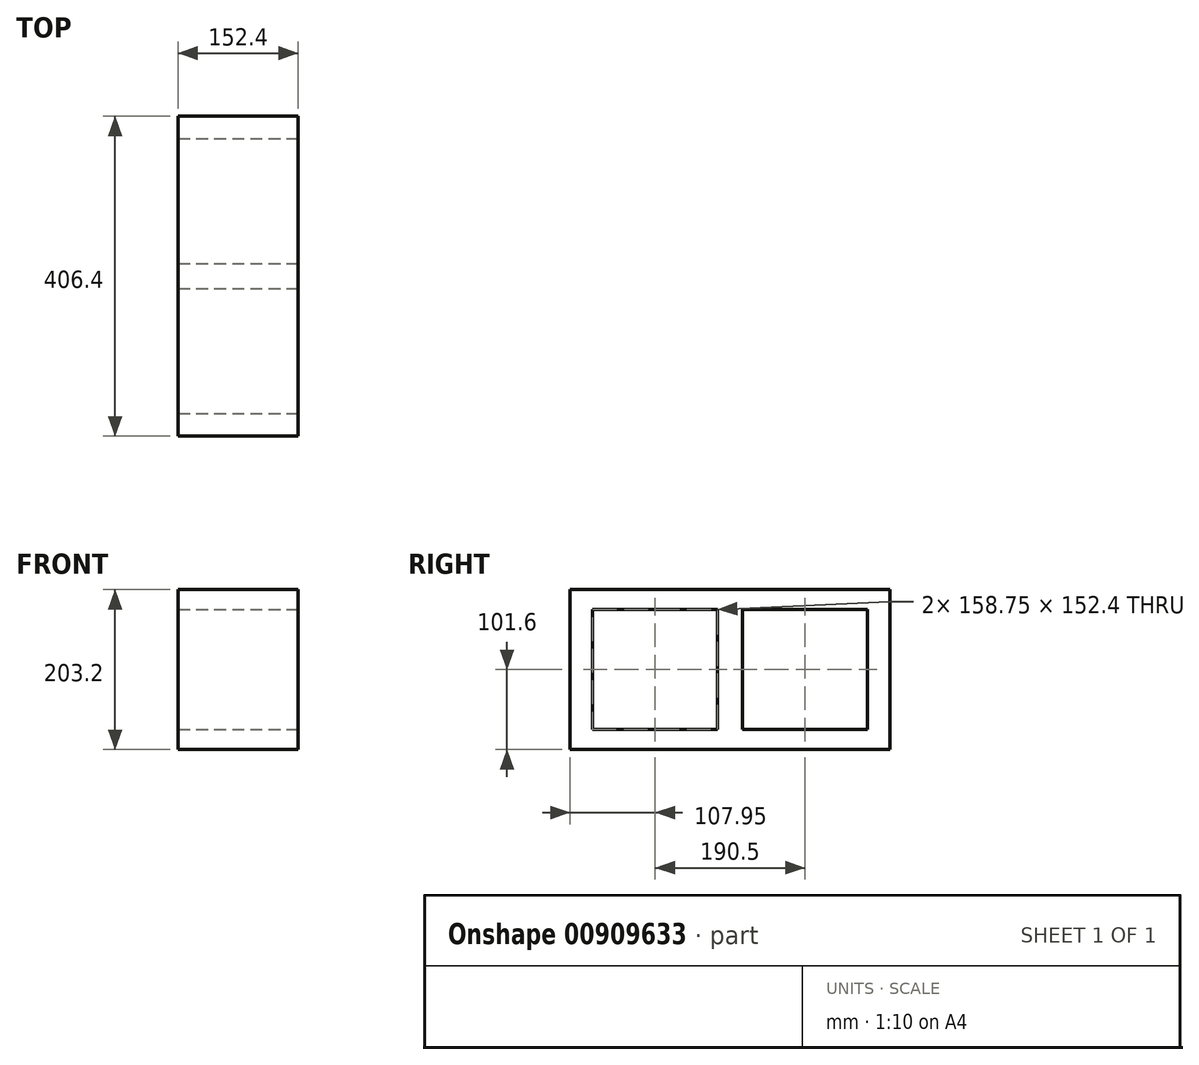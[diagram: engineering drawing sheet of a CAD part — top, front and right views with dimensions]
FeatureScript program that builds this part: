
annotation { "Feature Type Name" : "Feature", "Feature Type Description" : "" }
export const myFeature = defineFeature(function(context is Context, id is Id, definition is map)
    precondition{}
    {
        {
            var Q0;
            Q0=qCreatedBy(makeId("Right.planeOp"),FACE);
            var sketch = newSketch(context, id + "F0", { "sketchPlane" : qUnion([Q0])});
            skLineSegment(sketch, "E0.bottom", {"start": v(203.2, 101.6) * mm, "end": v(-203.2, 101.6) * mm});
            skLineSegment(sketch, "E0.top", {"start": v(203.2, -101.6) * mm, "end": v(-203.2, -101.6) * mm});
            skLineSegment(sketch, "E0.left", {"start": v(203.2, 101.6) * mm, "end": v(203.2, -101.6) * mm});
            skLineSegment(sketch, "E0.right", {"start": v(-203.2, 101.6) * mm, "end": v(-203.2, -101.6) * mm});
            skPoint(sketch, "E0.middle", {"position": v(0, 0) * mm});
            skLineSegment(sketch, "E1", {"start": v(0, 0) * mm, "end": v(95.25, 0) * mm, "construction": true});
            skLineSegment(sketch, "E2", {"start": v(0, 0) * mm, "end": v(-95.25, 0) * mm, "construction": true});
            skLineSegment(sketch, "E3.bottom", {"start": v(-174.63, 76.2) * mm, "end": v(-15.88, 76.2) * mm});
            skLineSegment(sketch, "E3.top", {"start": v(-174.63, -76.2) * mm, "end": v(-15.88, -76.2) * mm});
            skLineSegment(sketch, "E3.left", {"start": v(-174.63, 76.2) * mm, "end": v(-174.63, -76.2) * mm});
            skLineSegment(sketch, "E3.right", {"start": v(-15.88, 76.2) * mm, "end": v(-15.88, -76.2) * mm});
            skPoint(sketch, "E3.middle", {"position": v(-95.25, 0) * mm});
            skLineSegment(sketch, "E4.bottom", {"start": v(174.62, 76.2) * mm, "end": v(15.87, 76.2) * mm});
            skLineSegment(sketch, "E4.top", {"start": v(174.62, -76.2) * mm, "end": v(15.87, -76.2) * mm});
            skLineSegment(sketch, "E4.left", {"start": v(174.62, 76.2) * mm, "end": v(174.62, -76.2) * mm});
            skLineSegment(sketch, "E4.right", {"start": v(15.87, 76.2) * mm, "end": v(15.87, -76.2) * mm});
            skPoint(sketch, "E4.middle", {"position": v(95.25, 0) * mm});
            skLineSegment(sketch, "E5", {"start": v(-174.63, 76.2) * mm, "end": v(-203.2, 76.2) * mm, "construction": true});
            skLineSegment(sketch, "E6", {"start": v(174.62, 76.2) * mm, "end": v(203.2, 76.2) * mm, "construction": true});
            skLineSegment(sketch, "E7", {"start": v(-15.88, 76.2) * mm, "end": v(15.87, 76.2) * mm, "construction": true});
            skSolve(sketch);
        }
        {
            var Q0;
            Q0 = qSketchRegion(id + "F0", true);
            extrude(context, id + "F1", {"entities" : qUnion([Q0]), "depth" : -152.4 * mm, "offsetDistance" : 25.4 * mm});
        }
        {
            var Q0;
            Q0=makeQuery(id+"F0.imprint","IMPRINT",FACE,{"disambiguationData":[TD([[makeQuery(id+"F0.imprint","IMPRINT",EDGE,{"derivedFrom":sQuery(id+"F0.wireOp",EDGE,"E3.bottom")}),-1.0]])]});
            var Q1;
            Q1=makeQuery(id+"F0.imprint","IMPRINT",FACE,{"disambiguationData":[TD([[makeQuery(id+"F0.imprint","IMPRINT",EDGE,{"derivedFrom":sQuery(id+"F0.wireOp",EDGE,"E4.bottom")}),1.0]])]});
            extrude(context, id + "F2", {"entities" : qUnion([Q0, Q1]), "operationType" : NewBodyOperationType.REMOVE, "oppositeDirection" : true, "depth" : 152.4 * mm, "offsetDistance" : 25.4 * mm});
        }
    });
